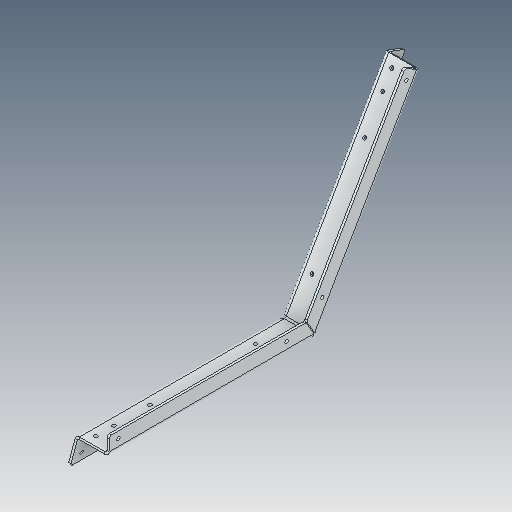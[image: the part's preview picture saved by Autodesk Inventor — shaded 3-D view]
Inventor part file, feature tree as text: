
AUTODESK INVENTOR PART (.ipt)
format: ipt  version: 2023.5 (Build 275446000, 446)  size: 173,568 bytes
history: native  units: in
note: dims shown in document units (in); Inventor stores cm internally (conversion verified against a paired STEP export)
features: mirror x1
ambient origin geometry x8: Origin, YZ Plane, XZ Plane, XY Plane, X Axis, Y Axis, Z Axis, Center Point
bodies: Solid1 (feature_tree)
feature tree (1):
  mirror  "Mirror1"
